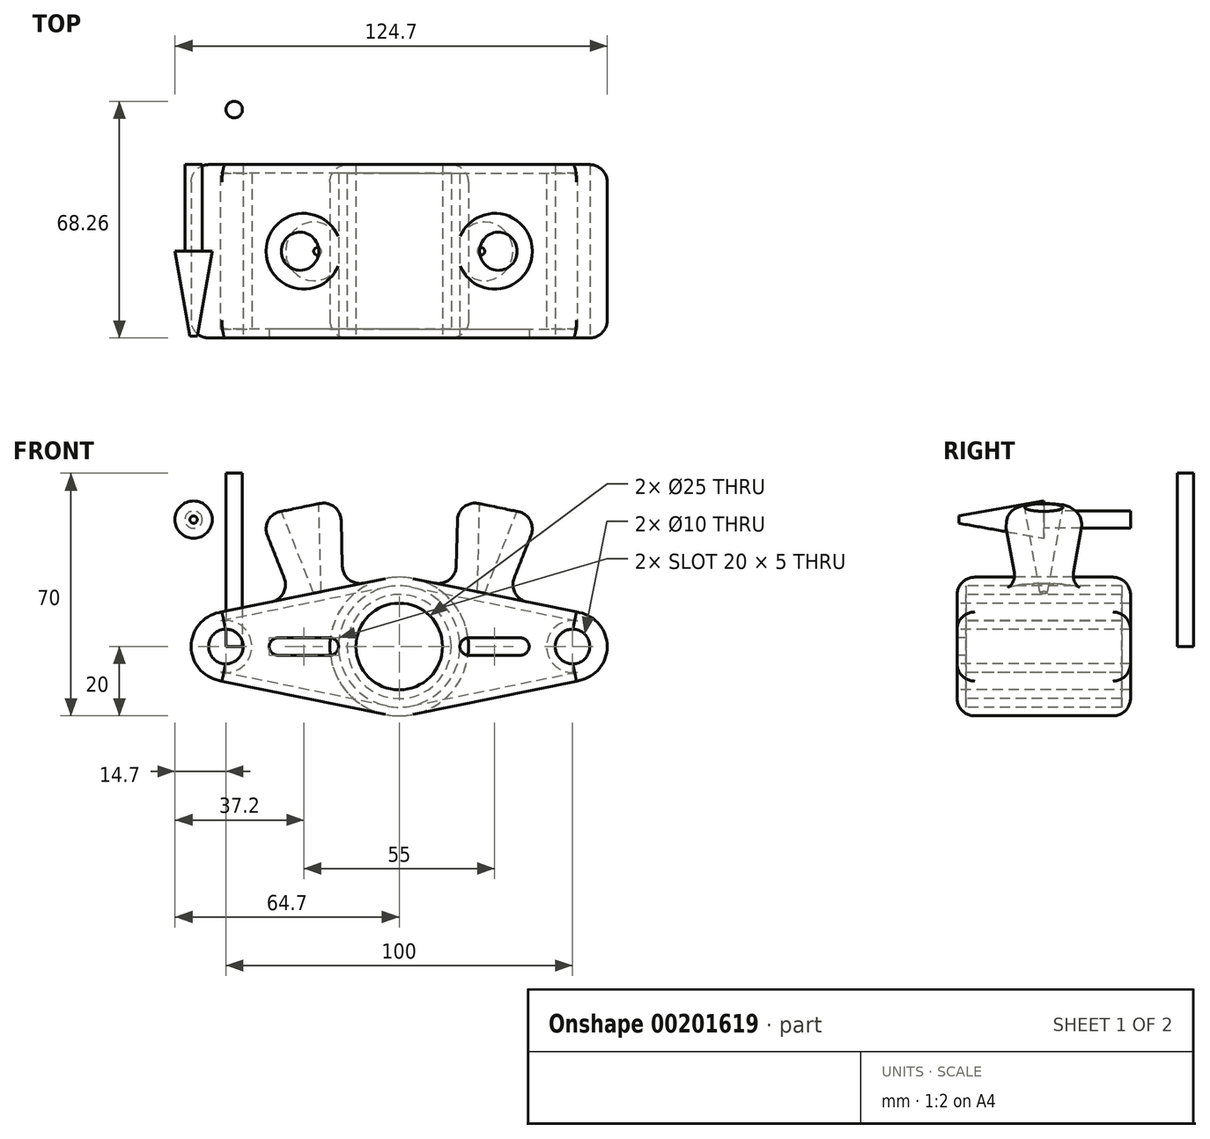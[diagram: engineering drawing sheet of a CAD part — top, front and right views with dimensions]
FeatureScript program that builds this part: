
annotation { "Feature Type Name" : "Feature", "Feature Type Description" : "" }
export const myFeature = defineFeature(function(context is Context, id is Id, definition is map)
    precondition{}
    {
        {
            var Q0;
            Q0=qCreatedBy(makeId("Front.planeOp"),FACE);
            var sketch = newSketch(context, id + "F0", { "sketchPlane" : qUnion([Q0])});
            skCircle(sketch, "E0", {"center": v(0, 0) * mm, "radius": 20 * mm});
            skCircle(sketch, "E1", {"center": v(50, 0) * mm, "radius": 10 * mm});
            skLineSegment(sketch, "E2", {"start": v(4, 19.6) * mm, "end": v(52, 9.8) * mm});
            skLineSegment(sketch, "E3", {"start": v(4, -19.6) * mm, "end": v(52, -9.8) * mm});
            skCircle(sketch, "E4", {"center": v(0, 0) * mm, "radius": 12.5 * mm});
            skCircle(sketch, "E5", {"center": v(50, 0) * mm, "radius": 5 * mm});
            skSolve(sketch);
        }
        {
            var Q0;
            Q0 = qSketchRegion(id + "F0", true);
            extrude(context, id + "F1", {"entities" : qUnion([Q0]), "endBound" : BoundingType.SYMMETRIC, "oppositeDirection" : true, "depth" : 50 * mm});
        }
        {
            var Q0;
            Q0=makeQuery(id+"F1.opExtrude","SWEPT_FACE",FACE,{"disambiguationData":[OSD([sQuery(id+"F0.wireOp",EDGE,"E2")])]});
            var sketch = newSketch(context, id + "F2", { "sketchPlane" : qUnion([Q0])});
            skCircle(sketch, "E6", {"center": v(20, 0) * mm, "radius": 7.5 * mm});
            skSolve(sketch);
        }
        {
            var Q0;
            Q0=makeQuery(id+"F1.opExtrude","CAP_FACE",FACE,{"disambiguationData":[OSD([sQuery(id+"F0.wireOp",EDGE,"E0"),sQuery(id+"F0.wireOp",EDGE,"E1"),sQuery(id+"F0.wireOp",EDGE,"E2"),sQuery(id+"F0.wireOp",EDGE,"E3"),sQuery(id+"F0.wireOp",EDGE,"E4"),sQuery(id+"F0.wireOp",EDGE,"E5")])],"isStart":true});
            var Q1;
            Q1=makeQuery(id+"F1.opExtrude","SWEPT_BODY",BODY,{"disambiguationData":[OSD([sQuery(id+"F0.wireOp",EDGE,"E0"),sQuery(id+"F0.wireOp",EDGE,"E1"),sQuery(id+"F0.wireOp",EDGE,"E2"),sQuery(id+"F0.wireOp",EDGE,"E3"),sQuery(id+"F0.wireOp",EDGE,"E4"),sQuery(id+"F0.wireOp",EDGE,"E5")])]});
            shell(context, id + "F3", {"isHollow" : true, "entities" : qUnion([Q0]), "parts" : qUnion([Q1]), "thickness" : 2.5 * mm});
        }
        {
            var Q0;
            Q0 = qSketchRegion(id + "F2", true);
            extrude(context, id + "F4", {"entities" : qUnion([Q0]), "operationType" : NewBodyOperationType.ADD, "depth" : 25 * mm, "hasDraft" : true, "draftAngle" : 10 * degree});
        }
        {
            var Q0;
            Q0=makeQuery(id+"F4.opExtrude","CAP_EDGE",EDGE,{"disambiguationData":[OSD([sQuery(id+"F2.wireOp",EDGE,"E6")])],"isStart":false});
            fillet(context, id + "F5", {"entities" : qUnion([Q0]), "radius" : 5.08 * mm, "tangentPropagation" : true, "allowEdgeOverflow" : false});
        }
        {
            var Q0;
            Q0=makeQuery(id+"F4.opExtrude","SWEPT_FACE",FACE,{"disambiguationData":[OSD([sQuery(id+"F2.wireOp",EDGE,"E6")])]});
            fillet(context, id + "F6", {"entities" : qUnion([Q0]), "radius" : 5.08 * mm, "tangentPropagation" : true, "allowEdgeOverflow" : false});
        }
        {
            var Q0;
            Q0=makeQuery(id+"F1.opExtrude","CAP_EDGE",EDGE,{"disambiguationData":[OSD([sQuery(id+"F0.wireOp",EDGE,"E0")])],"isStart":true});
            var Q1;
            Q1=makeQuery(id+"F1.opExtrude","CAP_EDGE",EDGE,{"disambiguationData":[OSD([sQuery(id+"F0.wireOp",EDGE,"E2")])],"isStart":false});
            fillet(context, id + "F7", {"entities" : qUnion([Q0, Q1]), "radius" : 5.08 * mm, "tangentPropagation" : true, "allowEdgeOverflow" : false});
        }
        {
            var Q0;
            Q0=makeQuery(id+"F4.opExtrude","CAP_FACE",FACE,{"disambiguationData":[OSD([sQuery(id+"F2.wireOp",EDGE,"E6")])],"isStart":false});
            var sketch = newSketch(context, id + "F8", { "sketchPlane" : qUnion([Q0])});
            skCircle(sketch, "E7", {"center": v(20, 0) * mm, "radius": 5.5 * mm});
            skSolve(sketch);
        }
        {
            var Q0;
            Q0 = qSketchRegion(id + "F8", true);
            extrude(context, id + "F9", {"entities" : qUnion([Q0]), "operationType" : NewBodyOperationType.REMOVE, "oppositeDirection" : true, "depth" : 25 * mm, "hasDraft" : true, "draftAngle" : 10 * degree, "draftPullDirection" : true});
        }
        {
            var Q0;
            Q0=qCreatedBy(makeId("Front.planeOp"),FACE);
            var sketch = newSketch(context, id + "F10", { "sketchPlane" : qUnion([Q0])});
            skCircle(sketch, "E8", {"center": v(-59.33, 36.6) * mm, "radius": 5.38 * mm});
            skSolve(sketch);
        }
        {
            var Q0;
            Q0=makeQuery(id+"F10.imprint","IMPRINT",FACE,{"disambiguationData":[TD([[makeQuery(id+"F10.imprint","IMPRINT",EDGE,{"derivedFrom":sQuery(id+"F10.wireOp",EDGE,"E8")}),1.0]])]});
            var Q1;
            Q1=sQuery(id+"F10.wireOp",EDGE,"E8");
            extrude(context, id + "F11", {"entities" : qUnion([Q0]), "surfaceEntities" : qUnion([Q1]), "depth" : 24.5 * mm, "hasDraft" : true, "draftAngle" : 10 * degree, "draftPullDirection" : true});
        }
        {
            var Q0;
            Q0=makeQuery(id+"F11.opExtrude","CAP_FACE",FACE,{"disambiguationData":[OSD([sQuery(id+"F10.wireOp",EDGE,"E8")])],"isStart":true});
            var sketch = newSketch(context, id + "F12", { "sketchPlane" : qUnion([Q0])});
            skCircle(sketch, "E9", {"center": v(59.33, 36.6) * mm, "radius": 2.5 * mm});
            skSolve(sketch);
        }
        {
            var Q0;
            Q0=makeQuery(id+"F12.imprint","IMPRINT",FACE,{"disambiguationData":[TD([[makeQuery(id+"F12.imprint","IMPRINT",EDGE,{"derivedFrom":sQuery(id+"F12.wireOp",EDGE,"E9")}),1.0]])]});
            extrude(context, id + "F13", {"entities" : qUnion([Q0]), "operationType" : NewBodyOperationType.ADD, "depth" : 25 * mm});
        }
        {
            var Q0;
            Q0=makeQuery(id+"F1.opExtrude","CAP_FACE",FACE,{"disambiguationData":[OSD([sQuery(id+"F0.wireOp",EDGE,"E0"),sQuery(id+"F0.wireOp",EDGE,"E1"),sQuery(id+"F0.wireOp",EDGE,"E2"),sQuery(id+"F0.wireOp",EDGE,"E3"),sQuery(id+"F0.wireOp",EDGE,"E4"),sQuery(id+"F0.wireOp",EDGE,"E5")])],"isStart":true});
            var sketch = newSketch(context, id + "F14", { "sketchPlane" : qUnion([Q0])});
            skCircle(sketch, "E10", {"center": v(20, 0) * mm, "radius": 2.5 * mm});
            skCircle(sketch, "E11", {"center": v(35, 0) * mm, "radius": 2.5 * mm});
            skLineSegment(sketch, "E12", {"start": v(20, 2.5) * mm, "end": v(35, 2.5) * mm});
            skLineSegment(sketch, "E13", {"start": v(20, -2.5) * mm, "end": v(35, -2.5) * mm});
            skSolve(sketch);
        }
        {
            var Q0;
            Q0 = qSketchRegion(id + "F14", true);
            extrude(context, id + "F15", {"entities" : qUnion([Q0]), "operationType" : NewBodyOperationType.REMOVE, "oppositeDirection" : true, "depth" : 25 * mm});
        }
        {
            var Q0;
            Q0=qCreatedBy(makeId("Top.planeOp"),FACE);
            var sketch = newSketch(context, id + "F16", { "sketchPlane" : qUnion([Q0])});
            skCircle(sketch, "E14", {"center": v(-47.6, 40.89) * mm, "radius": 2.38 * mm});
            skSolve(sketch);
        }
        {
            var Q0;
            Q0=makeQuery(id+"F16.imprint","IMPRINT",FACE,{"disambiguationData":[TD([[makeQuery(id+"F16.imprint","IMPRINT",EDGE,{"derivedFrom":sQuery(id+"F16.wireOp",EDGE,"E14")}),1.0]])]});
            extrude(context, id + "F17", {"entities" : qUnion([Q0]), "depth" : 50 * mm});
        }
        {
            var Q0;
            Q0=makeQuery(id+"F1.opExtrude","SWEPT_BODY",BODY,{"disambiguationData":[OSD([sQuery(id+"F0.wireOp",EDGE,"E0"),sQuery(id+"F0.wireOp",EDGE,"E1"),sQuery(id+"F0.wireOp",EDGE,"E2"),sQuery(id+"F0.wireOp",EDGE,"E3"),sQuery(id+"F0.wireOp",EDGE,"E4"),sQuery(id+"F0.wireOp",EDGE,"E5")])]});
            var Q1;
            Q1=qCreatedBy(makeId("Right.planeOp"),FACE);
            mirror(context, id + "F18", {"operationType" : NewBodyOperationType.ADD, "entities" : qUnion([Q0]), "mirrorPlane" : qUnion([Q1])});
        }
    });
